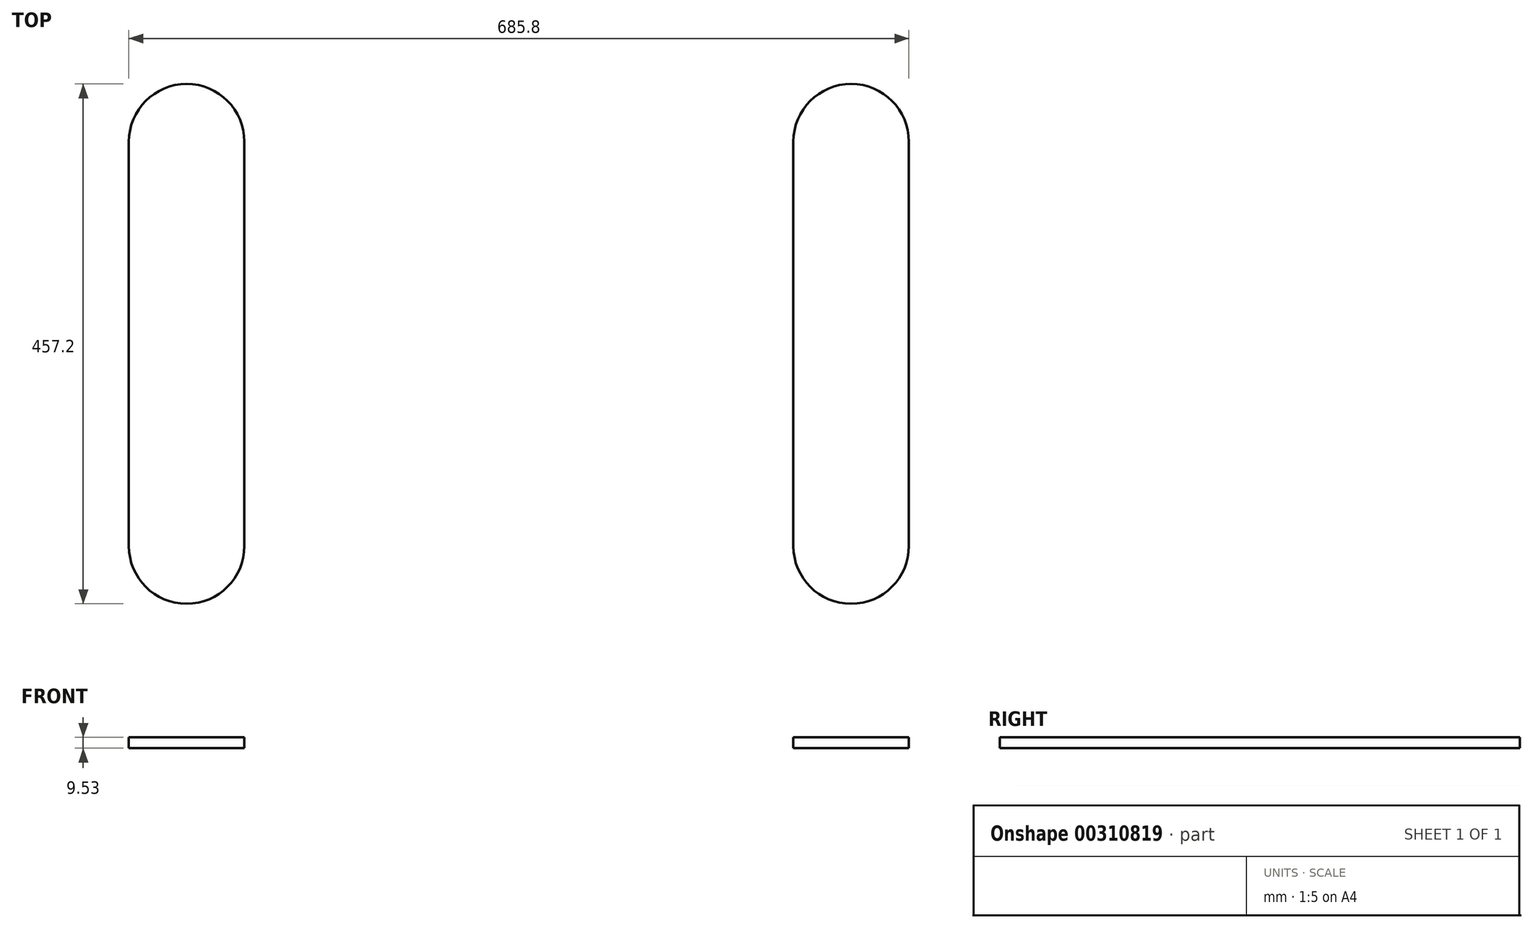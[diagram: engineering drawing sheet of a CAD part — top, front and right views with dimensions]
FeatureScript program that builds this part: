
annotation { "Feature Type Name" : "Feature", "Feature Type Description" : "" }
export const myFeature = defineFeature(function(context is Context, id is Id, definition is map)
    precondition{}
    {
        {
            var Q0;
            Q0=qCreatedBy(makeId("Top.planeOp"),FACE);
            var sketch = newSketch(context, id + "F0", { "sketchPlane" : qUnion([Q0])});
            skLineSegment(sketch, "E0.bottom", {"start": v(-256.09, 27.6) * mm, "end": v(-256.09, 27.6) * mm});
            skLineSegment(sketch, "E0.top", {"start": v(-256.09, -429.6) * mm, "end": v(-256.09, -429.6) * mm});
            skLineSegment(sketch, "E0.left", {"start": v(-306.89, -23.2) * mm, "end": v(-306.89, -378.8) * mm});
            skLineSegment(sketch, "E0.right", {"start": v(-205.29, -23.2) * mm, "end": v(-205.29, -378.8) * mm});
            skPoint(sketch, "E1.visualSharp", {"position": v(-306.89, 27.6) * mm});
            skArc(sketch, "E1.filletArc", {"start": v(-256.09, 27.6) * mm, "mid": v(-292, 12.72) * mm, "end": v(-306.89, -23.2) * mm});
            skPoint(sketch, "E2.visualSharp", {"position": v(-205.29, 27.6) * mm});
            skArc(sketch, "E2.filletArc", {"start": v(-205.29, -23.2) * mm, "mid": v(-220.16, 12.72) * mm, "end": v(-256.09, 27.6) * mm});
            skPoint(sketch, "E3.visualSharp", {"position": v(-306.89, -429.6) * mm});
            skArc(sketch, "E3.filletArc", {"start": v(-306.89, -378.8) * mm, "mid": v(-292, -414.72) * mm, "end": v(-256.09, -429.6) * mm});
            skPoint(sketch, "E4.visualSharp", {"position": v(-205.29, -429.6) * mm});
            skArc(sketch, "E4.filletArc", {"start": v(-256.09, -429.6) * mm, "mid": v(-220.16, -414.72) * mm, "end": v(-205.29, -378.8) * mm});
            skSolve(sketch);
        }
        {
            var Q0;
            Q0=makeQuery(id+"F0.imprint","IMPRINT",FACE,{"disambiguationData":[TD([[makeQuery(id+"F0.imprint","IMPRINT",EDGE,{"derivedFrom":sQuery(id+"F0.wireOp",EDGE,"E0.left")}),1.0]])]});
            extrude(context, id + "F1", {"entities" : qUnion([Q0]), "depth" : 9.52 * mm});
        }
        {
            var Q0;
            Q0=makeQuery(id+"F1.opExtrude","SWEPT_BODY",BODY,{"disambiguationData":[OSD([sQuery(id+"F0.wireOp",EDGE,"E0.left"),sQuery(id+"F0.wireOp",EDGE,"E0.right"),sQuery(id+"F0.wireOp",EDGE,"E1.filletArc"),sQuery(id+"F0.wireOp",EDGE,"E2.filletArc"),sQuery(id+"F0.wireOp",EDGE,"E3.filletArc"),sQuery(id+"F0.wireOp",EDGE,"E4.filletArc")])]});
            transform(context, id + "F2", {"entities" : qUnion([Q0]), "transformType" : TransformType.TRANSLATION_3D, "dx" : 220.98 * mm, "dy" : 0 * mm, "dz" : 0 * mm, "makeCopy" : true});
        }
        {
            var Q0;
            Q0=makeQuery(id+"F1.opExtrude","SWEPT_BODY",BODY,{"disambiguationData":[OSD([sQuery(id+"F0.wireOp",EDGE,"E0.left"),sQuery(id+"F0.wireOp",EDGE,"E0.right"),sQuery(id+"F0.wireOp",EDGE,"E1.filletArc"),sQuery(id+"F0.wireOp",EDGE,"E2.filletArc"),sQuery(id+"F0.wireOp",EDGE,"E3.filletArc"),sQuery(id+"F0.wireOp",EDGE,"E4.filletArc")])]});
            transform(context, id + "F3", {"entities" : qUnion([Q0]), "transformType" : TransformType.TRANSLATION_3D, "dx" : -363.22 * mm, "dy" : 0 * mm, "dz" : 0 * mm, "makeCopy" : false});
        }
    });
